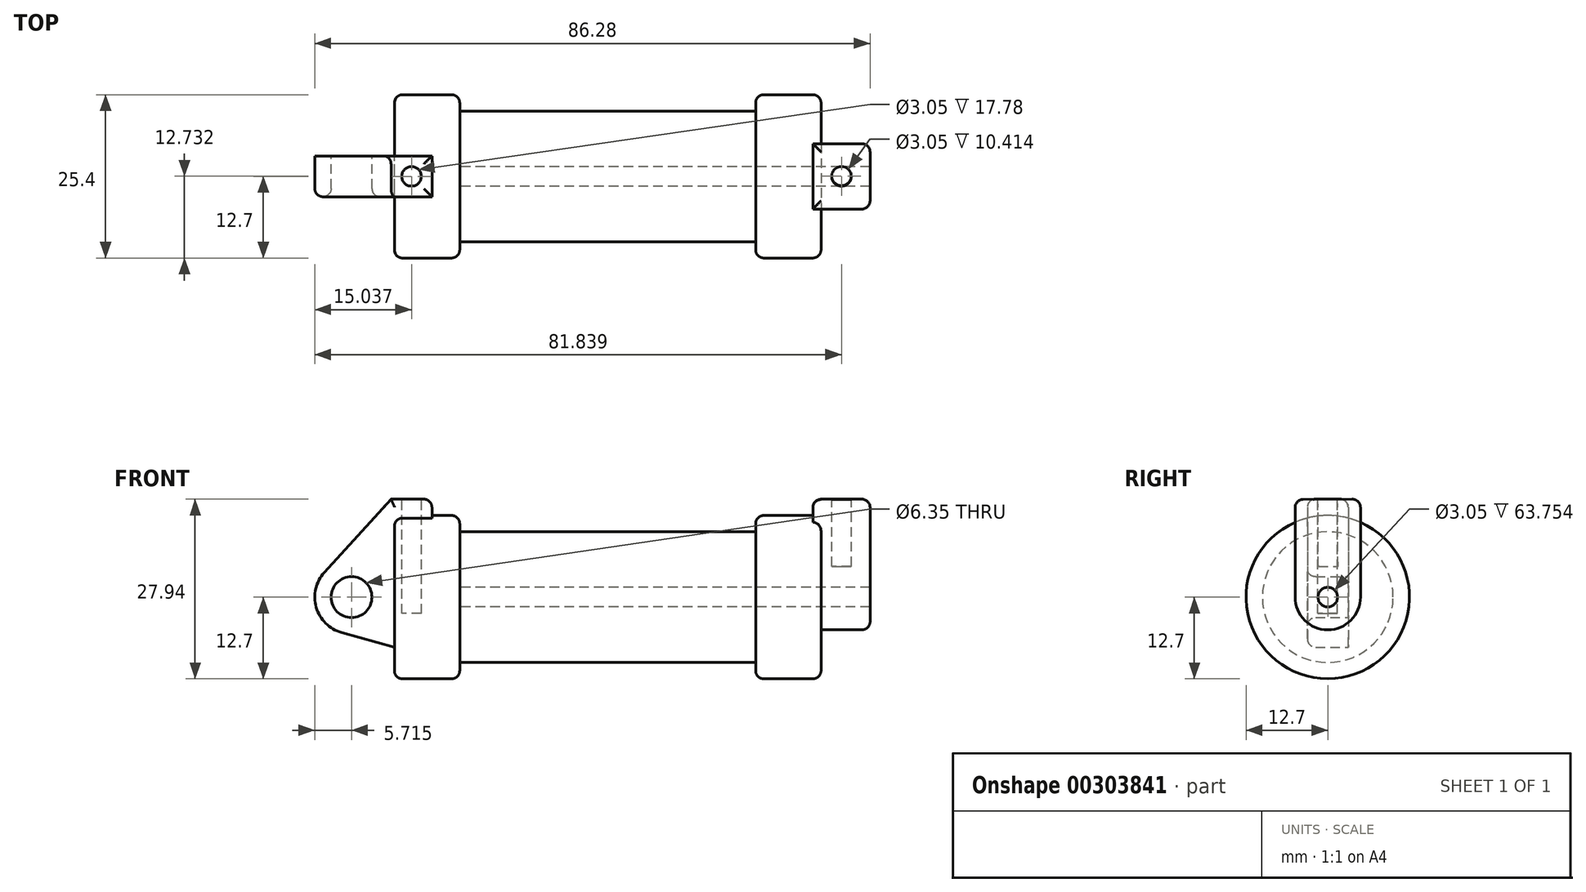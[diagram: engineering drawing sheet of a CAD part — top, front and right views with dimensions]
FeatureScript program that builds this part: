
annotation { "Feature Type Name" : "Feature", "Feature Type Description" : "" }
export const myFeature = defineFeature(function(context is Context, id is Id, definition is map)
    precondition{}
    {
        {
            var Q0;
            Q0=qCreatedBy(makeId("Front.planeOp"),FACE);
            var sketch = newSketch(context, id + "F0", { "sketchPlane" : qUnion([Q0])});
            skLineSegment(sketch, "E0", {"start": v(0, 0) * mm, "end": v(0, 12.7) * mm});
            skLineSegment(sketch, "E1", {"start": v(0, 12.7) * mm, "end": v(10.16, 12.7) * mm});
            skLineSegment(sketch, "E2", {"start": v(10.16, 12.7) * mm, "end": v(10.16, 10.16) * mm});
            skLineSegment(sketch, "E3", {"start": v(10.16, 10.16) * mm, "end": v(56.13, 10.16) * mm});
            skLineSegment(sketch, "E4", {"start": v(56.13, 10.16) * mm, "end": v(56.13, 12.7) * mm});
            skLineSegment(sketch, "E5", {"start": v(56.13, 12.7) * mm, "end": v(66.3, 12.7) * mm});
            skLineSegment(sketch, "E6", {"start": v(66.3, 12.7) * mm, "end": v(66.3, 0) * mm});
            skLineSegment(sketch, "E7", {"start": v(66.3, 0) * mm, "end": v(0, 0) * mm});
            skLineSegment(sketch, "E8", {"start": v(5.84, 15.24) * mm, "end": v(-0.5, 15.24) * mm});
            skLineSegment(sketch, "E9", {"start": v(-0.5, 15.24) * mm, "end": v(-10.88, 3.85) * mm});
            skLineSegment(sketch, "E10", {"start": v(0, 0) * mm, "end": v(-6.65, 0) * mm});
            skCircle(sketch, "E11", {"center": v(-6.65, 0) * mm, "radius": 5.72 * mm});
            skCircle(sketch, "E12", {"center": v(-6.65, 0) * mm, "radius": 3.18 * mm});
            skLineSegment(sketch, "E13", {"start": v(5.84, 15.24) * mm, "end": v(5.84, -9.4) * mm});
            skLineSegment(sketch, "E14", {"start": v(5.84, -9.4) * mm, "end": v(-8.18, -5.5) * mm});
            skSolve(sketch);
        }
        {
            var Q0;
            {var subQ0=sQuery(id+"F0.wireOp",EDGE,"E2");Q0=makeQuery(id+"F0.imprint","IMPRINT",FACE,{"disambiguationData":[TD([[makeQuery(id+"F0.imprint","IMPRINT",EDGE,{"derivedFrom":subQ0}),-1.0]])]});}
            var Q1;
            {var subQ0=sQuery(id+"F0.wireOp",EDGE,"E0");Q1=makeQuery(id+"F0.imprint","IMPRINT",FACE,{"disambiguationData":[TD([[makeQuery(id+"F0.imprint","IMPRINT",EDGE,{"derivedFrom":subQ0}),-1.0]])]});}
            var Q2;
            Q2=sQuery(id+"F0.wireOp",EDGE,"E7");
            revolve(context, id + "F1", {"entities" : qUnion([Q0, Q1]), "axis" : qUnion([Q2]), "revolveType" : RevolveType.FULL});
        }
        {
            var Q0;
            {var subQ1=sQuery(id+"F0.wireOp",EDGE,"E0");Q0=makeQuery(id+"F0.imprint","IMPRINT",FACE,{"disambiguationData":[TD([[makeQuery(id+"F0.imprint","IMPRINT",EDGE,{"derivedFrom":subQ1}),1.0]])]});}
            var Q1;
            {var subQ0=sQuery(id+"F0.wireOp",EDGE,"E0");Q1=makeQuery(id+"F0.imprint","IMPRINT",FACE,{"disambiguationData":[TD([[makeQuery(id+"F0.imprint","IMPRINT",EDGE,{"derivedFrom":subQ0}),-1.0]])]});}
            var Q2;
            {var subQ0=sQuery(id+"F0.wireOp",EDGE,"E14");Q2=makeQuery(id+"F0.imprint","IMPRINT",FACE,{"disambiguationData":[TD([[makeQuery(id+"F0.imprint","IMPRINT",EDGE,{"derivedFrom":subQ0}),-1.0]])]});}
            var Q3;
            {var subQ5=sQuery(id+"F0.wireOp",EDGE,"E12");Q3=makeQuery(id+"F0.imprint","IMPRINT",FACE,{"disambiguationData":[TD([[makeQuery(id+"F0.imprint","IMPRINT",EDGE,{"derivedFrom":subQ5}),-1.0]])]});}
            extrude(context, id + "F2", {"entities" : qUnion([Q0, Q1, Q2, Q3]), "operationType" : NewBodyOperationType.ADD, "endBound" : BoundingType.SYMMETRIC, "depth" : 6.35 * mm});
        }
        {
            var Q0;
            Q0=makeQuery(id+"F1.opRevolve","SWEPT_FACE",FACE,{"disambiguationData":[OSD([sQuery(id+"F0.wireOp",EDGE,"E6")])]});
            var sketch = newSketch(context, id + "F3", { "sketchPlane" : qUnion([Q0])});
            skCircle(sketch, "E15", {"center": v(0, 0) * mm, "radius": 1.52 * mm});
            skCircle(sketch, "E16", {"center": v(0, 0) * mm, "radius": 5.08 * mm});
            skLineSegment(sketch, "E17", {"start": v(-5.08, 0) * mm, "end": v(-5.08, 15.18) * mm});
            skLineSegment(sketch, "E18", {"start": v(5.08, 0) * mm, "end": v(5.08, 15.24) * mm});
            skLineSegment(sketch, "E19", {"start": v(5.08, 15.24) * mm, "end": v(-5.08, 15.18) * mm});
            skSolve(sketch);
        }
        {
            var Q0;
            {var subQ0=sQuery(id+"F3.wireOp",EDGE,"E19");Q0=makeQuery(id+"F3.imprint","IMPRINT",FACE,{"disambiguationData":[TD([[makeQuery(id+"F3.imprint","IMPRINT",EDGE,{"derivedFrom":subQ0}),1.0]])]});}
            var Q1;
            {var subQ0=sQuery(id+"F3.wireOp",EDGE,"E17");var subQ1=sQuery(id+"F3.wireOp",EDGE,"E16");var subQ2=makeQuery(id+"F3.imprint","INTERSECT",VERTEX,{"derivedFrom":[subQ1,subQ0]});Q1=makeQuery(id+"F3.imprint","IMPRINT",FACE,{"disambiguationData":[TD([[makeQuery(id+"F3.imprint","IMPRINT",EDGE,{"disambiguationData":[TD([[subQ2,1.0]])],"derivedFrom":subQ1}),-1.0]])]});}
            var Q2;
            Q2=makeQuery(id+"F3.imprint","IMPRINT",FACE,{"disambiguationData":[TD([[makeQuery(id+"F3.imprint","IMPRINT",EDGE,{"derivedFrom":sQuery(id+"F3.wireOp",EDGE,"E15")}),-1.0]])]});
            extrude(context, id + "F4", {"entities" : qUnion([Q0, Q1, Q2]), "operationType" : NewBodyOperationType.ADD, "depth" : 7.62 * mm, "hasSecondDirection" : true, "secondDirectionOppositeDirection" : true, "secondDirectionDepth" : 1.27 * mm});
        }
        {
            var Q0;
            Q0=makeQuery(id+"F4.boolean.opBoolean","SPLIT",FACE,{"disambiguationData":[TD([makeQuery(id+"F4.opExtrude","SWEPT_FACE",FACE,{"disambiguationData":[OSD([sQuery(id+"F3.wireOp",EDGE,"E15")])]})])],"derivedFrom":makeQuery(id+"F1.opRevolve","SWEPT_FACE",FACE,{"disambiguationData":[OSD([sQuery(id+"F0.wireOp",EDGE,"E6")])]})});
            var Q1;
            Q1=makeQuery(id+"F1.opRevolve","SWEPT_FACE",FACE,{"disambiguationData":[OSD([sQuery(id+"F0.wireOp",EDGE,"E2")])]});
            extrude(context, id + "F5", {"entities" : qUnion([Q0]), "operationType" : NewBodyOperationType.REMOVE, "endBound" : BoundingType.UP_TO_SURFACE, "oppositeDirection" : true, "endBoundEntityFace" : qUnion([Q1]), "depth" : 25.4 * mm});
        }
        {
            var Q0;
            Q0=makeQuery(id+"F2.opExtrude","SWEPT_FACE",FACE,{"disambiguationData":[OSD([sQuery(id+"F0.wireOp",EDGE,"E8")])]});
            var sketch = newSketch(context, id + "F6", { "sketchPlane" : qUnion([Q0])});
            skCircle(sketch, "E20", {"center": v(2.67, 0) * mm, "radius": 1.52 * mm});
            skPoint(sketch, "E20.centerSnap0", {"position": v(2.67, -3.18) * mm});
            skPoint(sketch, "E20.centerSnap1", {"position": v(-0.5, 0) * mm});
            skSolve(sketch);
        }
        {
            var Q0;
            Q0=makeQuery(id+"F6.imprint","IMPRINT",FACE,{"disambiguationData":[TD([[makeQuery(id+"F6.imprint","IMPRINT",EDGE,{"derivedFrom":sQuery(id+"F6.wireOp",EDGE,"E20")}),1.0]])]});
            extrude(context, id + "F7", {"entities" : qUnion([Q0]), "operationType" : NewBodyOperationType.REMOVE, "oppositeDirection" : true, "depth" : 17.78 * mm});
        }
        {
            var Q0;
            Q0=makeQuery(id+"F4.opExtrude","SWEPT_FACE",FACE,{"disambiguationData":[OSD([sQuery(id+"F3.wireOp",EDGE,"E19")])]});
            var sketch = newSketch(context, id + "F8", { "sketchPlane" : qUnion([Q0])});
            skCircle(sketch, "E21", {"center": v(69.47, 0.1) * mm, "radius": 1.52 * mm});
            skPoint(sketch, "E21.centerSnap0", {"position": v(65.02, 0.1) * mm});
            skPoint(sketch, "E21.centerSnap1", {"position": v(69.47, -4.99) * mm});
            skSolve(sketch);
        }
        {
            var Q0;
            Q0 = qSketchRegion(id + "F8", true);
            extrude(context, id + "F9", {"entities" : qUnion([Q0]), "operationType" : NewBodyOperationType.REMOVE, "oppositeDirection" : true, "depth" : 10.4 * mm});
        }
        {
            var Q0;
            Q0=makeQuery(id+"F2.opExtrude","CAP_EDGE",EDGE,{"disambiguationData":[OSD([sQuery(id+"F0.wireOp",EDGE,"E8")])],"isStart":false});
            var Q1;
            Q1=makeQuery(id+"F2.opExtrude","CAP_EDGE",EDGE,{"disambiguationData":[OSD([sQuery(id+"F0.wireOp",EDGE,"E12")])],"isStart":false});
            var Q2;
            Q2=makeQuery(id+"F2.opExtrude","CAP_EDGE",EDGE,{"disambiguationData":[OSD([sQuery(id+"F0.wireOp",EDGE,"E11")])],"isStart":false});
            var Q3;
            Q3=makeQuery(id+"F2.opExtrude","CAP_EDGE",EDGE,{"disambiguationData":[OSD([sQuery(id+"F0.wireOp",EDGE,"E14")])],"isStart":false});
            var Q4;
            Q4=makeQuery(id+"F1.opRevolve","SWEPT_EDGE",EDGE,{"disambiguationData":[OSD([sQuery(id+"F0.wireOp",EDGE,"E0"),sQuery(id+"F0.wireOp",EDGE,"E1")])]});
            var Q5;
            Q5=makeQuery(id+"F1.opRevolve","SWEPT_EDGE",EDGE,{"disambiguationData":[OSD([sQuery(id+"F0.wireOp",EDGE,"E1"),sQuery(id+"F0.wireOp",EDGE,"E2")])]});
            var Q6;
            Q6=makeQuery(id+"F1.opRevolve","SWEPT_EDGE",EDGE,{"disambiguationData":[OSD([sQuery(id+"F0.wireOp",EDGE,"E4"),sQuery(id+"F0.wireOp",EDGE,"E5")])]});
            var Q7;
            Q7=makeQuery(id+"F4.opExtrude","SWEPT_EDGE",EDGE,{"disambiguationData":[OSD([sQuery(id+"F3.wireOp",EDGE,"E17"),sQuery(id+"F3.wireOp",EDGE,"E19")])]});
            var Q8;
            Q8=makeQuery(id+"F4.opExtrude","CAP_EDGE",EDGE,{"disambiguationData":[OSD([sQuery(id+"F3.wireOp",EDGE,"E17")])],"isStart":false});
            var Q9;
            Q9=makeQuery(id+"F4.opExtrude","CAP_EDGE",EDGE,{"disambiguationData":[OSD([sQuery(id+"F3.wireOp",EDGE,"E19")])],"isStart":false});
            var Q10;
            Q10=makeQuery(id+"F4.opExtrude","SWEPT_EDGE",EDGE,{"disambiguationData":[OSD([sQuery(id+"F3.wireOp",EDGE,"E18"),sQuery(id+"F3.wireOp",EDGE,"E19")])]});
            var Q11;
            Q11=makeQuery(id+"F4.opExtrude","CAP_EDGE",EDGE,{"disambiguationData":[OSD([sQuery(id+"F3.wireOp",EDGE,"E19")])],"isStart":true});
            var Q12;
            Q12=makeQuery(id+"F2.opExtrude","CAP_EDGE",EDGE,{"disambiguationData":[OSD([sQuery(id+"F0.wireOp",EDGE,"E8")])],"isStart":true});
            var Q13;
            Q13=makeQuery(id+"F2.opExtrude","SWEPT_EDGE",EDGE,{"disambiguationData":[OSD([sQuery(id+"F0.wireOp",EDGE,"E8"),sQuery(id+"F0.wireOp",EDGE,"E13")])]});
            var Q14;
            Q14=makeQuery(id+"F4.opExtrude","SWEPT_EDGE",EDGE,{"disambiguationData":[OSD([sQuery(id+"F3.wireOp",EDGE,"E16"),sQuery(id+"F3.wireOp",EDGE,"E17")])]});
            var Q15;
            Q15=makeQuery(id+"F2.opExtrude","CAP_EDGE",EDGE,{"disambiguationData":[OSD([sQuery(id+"F0.wireOp",EDGE,"E9")])],"isStart":false});
            var Q16;
            Q16=makeQuery(id+"F1.opRevolve","SWEPT_EDGE",EDGE,{"disambiguationData":[OSD([sQuery(id+"F0.wireOp",EDGE,"E5"),sQuery(id+"F0.wireOp",EDGE,"E6")])]});
            fillet(context, id + "F10", {"entities" : qUnion([Q0, Q1, Q2, Q3, Q4, Q5, Q6, Q7, Q8, Q9, Q10, Q11, Q12, Q13, Q14, Q15, Q16]), "radius" : 1.27 * mm, "tangentPropagation" : true, "allowEdgeOverflow" : false});
        }
    });
